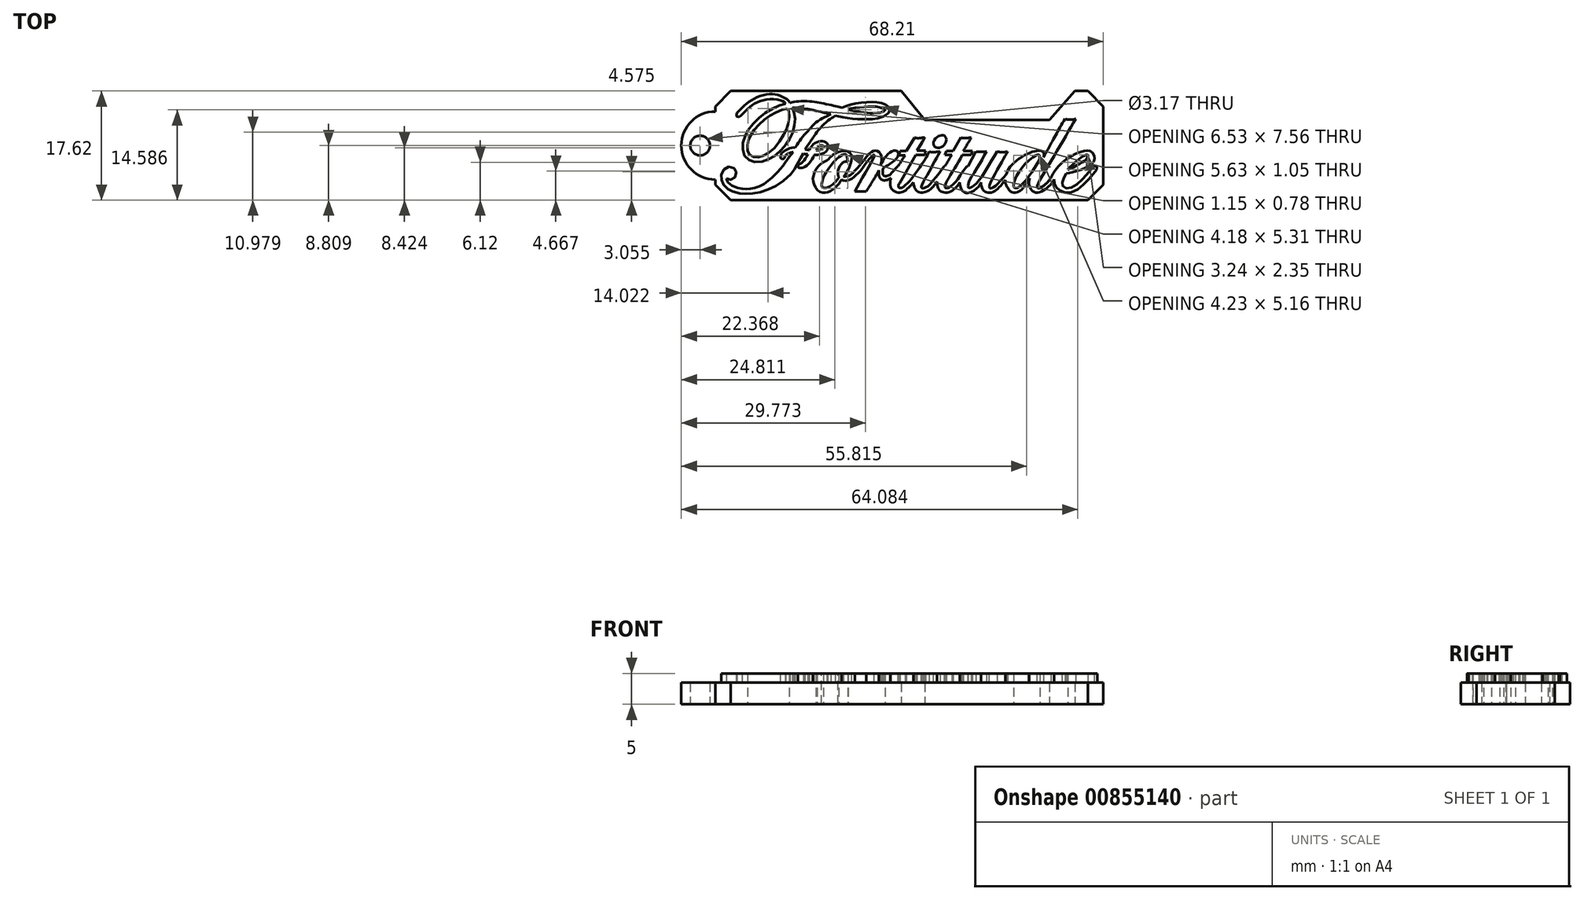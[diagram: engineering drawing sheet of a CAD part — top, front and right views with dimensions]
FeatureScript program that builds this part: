
annotation { "Feature Type Name" : "Feature", "Feature Type Description" : "" }
export const myFeature = defineFeature(function(context is Context, id is Id, definition is map)
    precondition{}
    {
        {
            var Q0;
            Q0=qCreatedBy(makeId("Top.planeOp"),FACE);
            var sketch = newSketch(context, id + "F0", { "sketchPlane" : qUnion([Q0])});
            skFitSpline(sketch, "E0", {"points": [v(-25.9, 14.46) * mm, v(-24.9, 15.47) * mm, v(-23.52, 16.57) * mm, v(-21.48, 17.37) * mm, v(-19.76, 17.48) * mm, v(-18.46, 17.05) * mm, v(-17.47, 16.4) * mm, v(-17.3, 16.1) * mm], "startDerivative": vector(6.68, 6.85) * mm, "endDerivative": vector(1.52, -4.02) * mm});
            skFitSpline(sketch, "E1", {"points": [v(-17.3, 16.1) * mm, v(-16.07, 16.32) * mm, v(-13.99, 16.32) * mm, v(-12.43, 16.1) * mm, v(-10.7, 15.75) * mm, v(-9.45, 15.46) * mm, v(-8.92, 15.33) * mm], "startDerivative": vector(7, 1.67) * mm, "endDerivative": vector(4.54, -1.1) * mm});
            skFitSpline(sketch, "E2", {"points": [v(-8.92, 15.33) * mm, v(-7.8, 15.72) * mm, v(-6.03, 16.1) * mm, v(-4.22, 16.24) * mm, v(-2.81, 16.1) * mm, v(-1.75, 15.75) * mm, v(-1.22, 15.17) * mm, v(-1.42, 14.43) * mm, v(-3.23, 13.6) * mm, v(-4.75, 13.45) * mm, v(-6.34, 13.45) * mm, v(-7.96, 13.65) * mm, v(-9.16, 13.89) * mm, v(-10, 14.03) * mm], "startDerivative": vector(14.5, 5.42) * mm, "endDerivative": vector(-13.1, 2.1) * mm});
            skFitSpline(sketch, "E3", {"points": [v(-10.72, 14.27) * mm, v(-11.87, 14.53) * mm, v(-14.18, 15.04) * mm, v(-15.29, 15.19) * mm, v(-16.51, 15.3) * mm, v(-16.96, 15.28) * mm], "startDerivative": vector(-5.05, 1.09) * mm, "endDerivative": vector(-3.1, -0.28) * mm});
            skFitSpline(sketch, "E4", {"points": [v(-16.96, 15.28) * mm, v(-16.76, 14.83) * mm, v(-16.53, 13.88) * mm, v(-16.54, 13) * mm, v(-16.75, 11.72) * mm, v(-17.21, 10.57) * mm, v(-17.81, 9.59) * mm, v(-18.53, 8.72) * mm, v(-19.73, 7.57) * mm, v(-21, 6.88) * mm, v(-22.1, 6.59) * mm, v(-23.33, 6.61) * mm, v(-24.04, 6.97) * mm, v(-24.7, 7.63) * mm, v(-24.96, 8.7) * mm, v(-24.88, 9.85) * mm, v(-24.48, 10.92) * mm, v(-23.96, 11.89) * mm, v(-22.83, 13.18) * mm, v(-21.63, 14.24) * mm, v(-20.17, 15.17) * mm, v(-18.93, 15.71) * mm, v(-18.07, 15.96) * mm], "startDerivative": vector(6.49, -13.43) * mm, "endDerivative": vector(20.82, 5.37) * mm});
            skFitSpline(sketch, "E5", {"points": [v(-18, 15.96) * mm, v(-18.48, 16.35) * mm, v(-19.96, 16.71) * mm, v(-21.78, 16.5) * mm, v(-23.11, 15.96) * mm, v(-24.23, 15.07) * mm, v(-24.97, 14.28) * mm, v(-25.45, 13.84) * mm, v(-25.72, 13.82) * mm, v(-25.96, 14) * mm, v(-25.9, 14.46) * mm], "startDerivative": vector(-4.62, 4.86) * mm, "endDerivative": vector(2.06, 7.08) * mm});
            skFitSpline(sketch, "E6", {"points": [v(-17.77, 15.15) * mm, v(-19, 14.84) * mm, v(-20.47, 14.1) * mm, v(-22.02, 12.88) * mm, v(-23.32, 11.43) * mm, v(-23.95, 10.22) * mm, v(-24.16, 9.36) * mm, v(-24.13, 8.22) * mm, v(-23.87, 7.8) * mm, v(-23.12, 7.33) * mm, v(-22.13, 7.4) * mm, v(-20.98, 7.9) * mm, v(-19.38, 9.33) * mm, v(-18.07, 11.42) * mm, v(-17.73, 12.26) * mm, v(-17.44, 14.12) * mm, v(-17.62, 15) * mm, v(-17.77, 15.15) * mm]});
            skFitSpline(sketch, "E7", {"points": [v(-10.72, 14.27) * mm, v(-11.48, 13.89) * mm, v(-13.02, 13) * mm, v(-14.3, 11.72) * mm, v(-15.48, 10.35) * mm, v(-16.31, 9.12) * mm, v(-16.48, 8.84) * mm], "startDerivative": vector(-4.97, -2.53) * mm, "endDerivative": vector(-1.64, -2.65) * mm});
            skFitSpline(sketch, "E8", {"points": [v(-16.48, 8.84) * mm, v(-17.1, 8.84) * mm, v(-18.12, 8.39) * mm, v(-18.69, 7.91) * mm, v(-18.87, 7.44) * mm, v(-18.78, 7.13) * mm, v(-18.55, 7) * mm, v(-18.31, 7.08) * mm, v(-18.18, 7.3) * mm, v(-17.96, 7.6) * mm, v(-17.76, 7.85) * mm, v(-17.42, 8.01) * mm, v(-17.05, 8.1) * mm, v(-16.78, 8.15) * mm], "startDerivative": vector(-6.16, 0.8) * mm, "endDerivative": vector(4.12, 0.95) * mm});
            skFitSpline(sketch, "E9", {"points": [v(-16.78, 8.15) * mm, v(-17.38, 7.46) * mm, v(-17.91, 6.68) * mm, v(-18.76, 5.56) * mm, v(-19.67, 4.55) * mm, v(-21.15, 3.25) * mm, v(-23.15, 2.32) * mm, v(-24.75, 2.2) * mm, v(-26.17, 2.48) * mm, v(-26.82, 2.8) * mm, v(-27.23, 3.16) * mm, v(-27.52, 3.62) * mm, v(-27.58, 3.89) * mm], "startDerivative": vector(-8.16, -8.88) * mm, "endDerivative": vector(-0.98, 5.99) * mm});
            skFitSpline(sketch, "E10", {"points": [v(-27.58, 3.89) * mm, v(-27.34, 3.7) * mm, v(-26.64, 3.73) * mm, v(-26.27, 4.04) * mm, v(-26, 4.66) * mm, v(-26.07, 5.08) * mm, v(-26.26, 5.44) * mm, v(-26.74, 5.72) * mm, v(-27.58, 5.67) * mm, v(-28.09, 5.2) * mm, v(-28.39, 4.53) * mm, v(-28.4, 3.92) * mm, v(-28.28, 3.27) * mm, v(-28.04, 2.84) * mm, v(-27.43, 2.22) * mm, v(-26.89, 1.92) * mm, v(-25.9, 1.55) * mm, v(-24.94, 1.4) * mm, v(-24.1, 1.4) * mm, v(-22.97, 1.48) * mm, v(-21.64, 1.78) * mm, v(-20.07, 2.43) * mm, v(-18.7, 3.25) * mm, v(-17.08, 4.7) * mm, v(-16.67, 5.27) * mm, v(-16.3, 5.9) * mm, v(-15.83, 6.72) * mm, v(-15.26, 7.74) * mm, v(-15.15, 7.91) * mm], "startDerivative": vector(8.41, -9.84) * mm, "endDerivative": vector(5.08, 7.16) * mm});
            skFitSpline(sketch, "E11", {"points": [v(-15.15, 7.91) * mm, v(-14.97, 7.84) * mm, v(-14.74, 7.84) * mm, v(-14.44, 7.81) * mm], "startDerivative": vector(0.56, -0.3) * mm, "endDerivative": vector(0.82, -0.1) * mm});
            skFitSpline(sketch, "E12", {"points": [v(-14.44, 7.81) * mm, v(-14.57, 7.49) * mm, v(-15, 6.82) * mm, v(-15.53, 6.32) * mm, v(-15.83, 6.19) * mm, v(-15.96, 6.08) * mm, v(-16.03, 5.86) * mm, v(-15.9, 5.62) * mm, v(-15.6, 5.56) * mm, v(-15.25, 5.65) * mm, v(-14.75, 5.86) * mm, v(-13.9, 6.76) * mm, v(-13.48, 7.48) * mm, v(-13.43, 7.68) * mm], "startDerivative": vector(-1.5, -4.37) * mm, "endDerivative": vector(0.64, 3.35) * mm});
            skFitSpline(sketch, "E13", {"points": [v(-13.43, 7.68) * mm, v(-12.95, 7.68) * mm, v(-12.29, 7.81) * mm, v(-11.5, 8.24) * mm, v(-11.22, 8.72) * mm, v(-11.2, 9.18) * mm, v(-11.34, 9.56) * mm, v(-11.65, 9.8) * mm, v(-12.12, 9.9) * mm, v(-12.69, 9.86) * mm, v(-13.25, 9.6) * mm, v(-13.7, 9.24) * mm, v(-14, 8.8) * mm, v(-14.18, 8.46) * mm], "startDerivative": vector(6.38, -0.23) * mm, "endDerivative": vector(-2.47, -4.89) * mm});
            skFitSpline(sketch, "E14", {"points": [v(-14.18, 8.46) * mm, v(-14.4, 8.51) * mm, v(-14.9, 8.56) * mm], "startDerivative": vector(-0.5, 0.14) * mm, "endDerivative": vector(-0.9, 0.07) * mm});
            skFitSpline(sketch, "E15", {"points": [v(-14.9, 8.56) * mm, v(-14.6, 9.02) * mm, v(-14.12, 9.74) * mm, v(-13.61, 10.44) * mm, v(-12.97, 11.37) * mm, v(-11.47, 12.96) * mm, v(-10.4, 13.76) * mm, v(-10, 14.03) * mm], "startDerivative": vector(2.69, 4.04) * mm, "endDerivative": vector(3.63, 2.41) * mm});
            skFitSpline(sketch, "E16", {"points": [v(-13.1, 8.44) * mm, v(-12.86, 8.84) * mm, v(-12.6, 9.06) * mm, v(-12.3, 9.2) * mm, v(-12, 9.16) * mm, v(-11.91, 9.03) * mm, v(-12, 8.82) * mm, v(-12.19, 8.63) * mm, v(-12.53, 8.47) * mm, v(-12.96, 8.42) * mm], "startDerivative": vector(1.62, 3.25) * mm, "endDerivative": vector(-3.32, -0.15) * mm});
            skFitSpline(sketch, "E17", {"points": [v(-12.96, 8.42) * mm, v(-13.1, 8.44) * mm], "startDerivative": vector(-0.14, 0.02) * mm, "endDerivative": vector(-0.14, 0.02) * mm});
            skFitSpline(sketch, "E18", {"points": [v(-7.93, 15.04) * mm, v(-7.1, 15.24) * mm, v(-5.76, 15.43) * mm, v(-4.6, 15.5) * mm, v(-3.4, 15.47) * mm, v(-2.45, 15.24) * mm, v(-1.95, 14.98) * mm, v(-2.02, 14.85) * mm, v(-2.26, 14.72) * mm, v(-2.6, 14.56) * mm, v(-2.88, 14.49) * mm, v(-3.54, 14.45) * mm, v(-4.4, 14.44) * mm, v(-5.03, 14.5) * mm, v(-5.97, 14.63) * mm, v(-6.66, 14.75) * mm, v(-7.62, 14.91) * mm, v(-7.93, 15.04) * mm]});
            skFitSpline(sketch, "E19", {"points": [v(-11.34, 6.78) * mm, v(-12.14, 6.36) * mm, v(-13, 5.56) * mm, v(-13.56, 4.23) * mm, v(-13.5, 3.23) * mm, v(-12.79, 1.93) * mm, v(-11.89, 1.6) * mm, v(-10.96, 1.76) * mm, v(-10.06, 2.33) * mm, v(-9.37, 3.13) * mm, v(-9, 3.71) * mm], "startDerivative": vector(-8.7, -4) * mm, "endDerivative": vector(4.14, 6.88) * mm});
            skFitSpline(sketch, "E20", {"points": [v(-11.34, 6.78) * mm, v(-10.7, 7.4) * mm, v(-9.66, 8.1) * mm, v(-8.28, 8.35) * mm, v(-7.53, 7.93) * mm, v(-7.35, 7.05) * mm, v(-7.6, 6) * mm, v(-8.22, 4.77) * mm, v(-8.7, 4.13) * mm], "startDerivative": vector(5.23, 5.36) * mm, "endDerivative": vector(-4.35, -5.22) * mm});
            skFitSpline(sketch, "E21", {"points": [v(-8, 6.63) * mm, v(-8.07, 7.24) * mm, v(-8.17, 7.6) * mm, v(-8.54, 7.79) * mm, v(-9.4, 7.35) * mm, v(-10.6, 6.12) * mm, v(-11.63, 4.61) * mm, v(-12.08, 3.55) * mm, v(-12.18, 2.56) * mm, v(-11.9, 2.33) * mm, v(-11.04, 2.46) * mm, v(-9.8, 3.5) * mm, v(-9.43, 4.03) * mm], "startDerivative": vector(-1.3, 9.27) * mm, "endDerivative": vector(4.03, 6.68) * mm});
            skFitSpline(sketch, "E22", {"points": [v(-9.43, 4.03) * mm, v(-9.53, 4.39) * mm, v(-9.53, 5.3) * mm, v(-9.11, 6.12) * mm, v(-8.66, 6.53) * mm, v(-8, 6.63) * mm], "startDerivative": vector(-0.69, 2.08) * mm, "endDerivative": vector(3.63, 0.09) * mm});
            skFitSpline(sketch, "E23", {"points": [v(-8.7, 4.13) * mm, v(-7.75, 4.34) * mm, v(-6.64, 5.33) * mm, v(-5.55, 6.63) * mm, v(-4.65, 7.73) * mm, v(-3.8, 8.36) * mm, v(-3.13, 8.27) * mm, v(-2.66, 7.84) * mm, v(-2.5, 7) * mm, v(-2.72, 5.96) * mm], "startDerivative": vector(9.04, 0.75) * mm, "endDerivative": vector(-2.78, -9.43) * mm});
            skFitSpline(sketch, "E24", {"points": [v(-2.72, 5.96) * mm, v(-2.3, 6.78) * mm, v(-1.3, 7.98) * mm, v(-0.43, 8.38) * mm, v(0.06, 8.2) * mm, v(0.18, 7.68) * mm, v(-0.35, 6.88) * mm, v(-1.62, 5.96) * mm, v(-2.2, 5.62) * mm], "startDerivative": vector(2.82, 6.13) * mm, "endDerivative": vector(-4.83, -2.64) * mm});
            skFitSpline(sketch, "E25", {"points": [v(-2.2, 5.62) * mm, v(-2.32, 5.27) * mm, v(-2.33, 4.67) * mm, v(-2.08, 4.3) * mm, v(-1.49, 4.32) * mm, v(-0.98, 4.68) * mm, v(-0.34, 5.4) * mm, v(0.03, 5.78) * mm, v(0.16, 5.86) * mm], "startDerivative": vector(-1.27, -3) * mm, "endDerivative": vector(1.86, 0.75) * mm});
            skFitSpline(sketch, "E26", {"points": [v(0.16, 5.86) * mm, v(0.73, 6.78) * mm, v(1.3, 7.65) * mm], "startDerivative": vector(1.1, 1.84) * mm, "endDerivative": vector(1.16, 1.75) * mm});
            skLineSegment(sketch, "E27", {"start": v(1.3, 7.65) * mm, "end": v(0.26, 7.65) * mm});
            skLineSegment(sketch, "E28", {"start": v(0.26, 7.65) * mm, "end": v(0.5, 8.35) * mm});
            skLineSegment(sketch, "E29", {"start": v(0.5, 8.35) * mm, "end": v(1.5, 8.35) * mm});
            skLineSegment(sketch, "E30", {"start": v(1.5, 8.35) * mm, "end": v(2.81, 10.5) * mm});
            skFitSpline(sketch, "E31", {"points": [v(2.81, 10.5) * mm, v(3.28, 10.39) * mm, v(4.23, 10.5) * mm], "startDerivative": vector(1.03, -0.37) * mm, "endDerivative": vector(1.76, 0.33) * mm});
            skLineSegment(sketch, "E32", {"start": v(4.23, 10.5) * mm, "end": v(4.49, 10.56) * mm});
            skLineSegment(sketch, "E33", {"start": v(4.49, 10.56) * mm, "end": v(4, 9.71) * mm});
            skLineSegment(sketch, "E34", {"start": v(4, 9.71) * mm, "end": v(3.23, 8.38) * mm});
            skLineSegment(sketch, "E35", {"start": v(3.23, 8.38) * mm, "end": v(4.62, 8.38) * mm});
            skLineSegment(sketch, "E36", {"start": v(4.62, 8.38) * mm, "end": v(4.46, 7.72) * mm});
            skLineSegment(sketch, "E37", {"start": v(4.46, 7.72) * mm, "end": v(3.01, 7.72) * mm});
            skLineSegment(sketch, "E38", {"start": v(3.01, 7.72) * mm, "end": v(0.37, 3.14) * mm});
            skFitSpline(sketch, "E39", {"points": [v(0.37, 3.14) * mm, v(0.23, 2.83) * mm, v(0.24, 2.46) * mm, v(0.6, 2.35) * mm, v(1.33, 2.78) * mm, v(2.9, 4.63) * mm, v(4.62, 7.19) * mm, v(5.16, 8.24) * mm], "startDerivative": vector(-1.96, -3.45) * mm, "endDerivative": vector(2.89, 6.1) * mm});
            skFitSpline(sketch, "E40", {"points": [v(5.16, 8.24) * mm, v(5.41, 8.15) * mm, v(6.1, 8.15) * mm, v(6.94, 8.24) * mm], "startDerivative": vector(0.95, -0.43) * mm, "endDerivative": vector(2.04, 0.26) * mm});
            skFitSpline(sketch, "E41", {"points": [v(7.2, 10.84) * mm, v(6.54, 10.65) * mm, v(5.92, 9.9) * mm, v(5.93, 9.21) * mm, v(6.4, 8.84) * mm, v(7.19, 8.98) * mm, v(7.81, 9.6) * mm, v(7.92, 10.32) * mm, v(7.67, 10.76) * mm, v(7.2, 10.84) * mm]});
            skFitSpline(sketch, "E42", {"points": [v(6.94, 8.24) * mm, v(5.89, 6.32) * mm, v(4.68, 4.14) * mm, v(3.94, 2.7) * mm, v(3.98, 2.37) * mm, v(4.2, 2.29) * mm, v(4.62, 2.42) * mm, v(5.27, 2.93) * mm, v(7.32, 5.45) * mm, v(7.57, 5.85) * mm], "startDerivative": vector(-6.56, -11.95) * mm, "endDerivative": vector(2.07, 3.87) * mm});
            skFitSpline(sketch, "E43", {"points": [v(7.57, 5.85) * mm, v(7.73, 5.87) * mm], "startDerivative": vector(0.16, 0.03) * mm, "endDerivative": vector(0.16, 0.03) * mm});
            skFitSpline(sketch, "E44", {"points": [v(7.73, 5.87) * mm, v(8.4, 7) * mm, v(8.83, 7.68) * mm], "startDerivative": vector(1.24, 2.13) * mm, "endDerivative": vector(0.94, 1.47) * mm});
            skFitSpline(sketch, "E45", {"points": [v(8.83, 7.68) * mm, v(7.73, 7.68) * mm], "startDerivative": vector(-1.1, 0) * mm, "endDerivative": vector(-1.1, 0) * mm});
            skFitSpline(sketch, "E46", {"points": [v(7.73, 7.68) * mm, v(7.96, 8.35) * mm], "startDerivative": vector(0.23, 0.66) * mm, "endDerivative": vector(0.23, 0.66) * mm});
            skFitSpline(sketch, "E47", {"points": [v(7.96, 8.35) * mm, v(9.02, 8.35) * mm], "startDerivative": vector(1.06, 0) * mm, "endDerivative": vector(1.06, 0) * mm});
            skFitSpline(sketch, "E48", {"points": [v(9.02, 8.35) * mm, v(10.34, 10.54) * mm], "startDerivative": vector(1.32, 2.19) * mm, "endDerivative": vector(1.32, 2.19) * mm});
            skFitSpline(sketch, "E49", {"points": [v(10.34, 10.54) * mm, v(10.48, 10.44) * mm, v(11.31, 10.43) * mm, v(11.98, 10.47) * mm], "startDerivative": vector(0.5, -0.58) * mm, "endDerivative": vector(1.58, 0.1) * mm});
            skFitSpline(sketch, "E50", {"points": [v(11.98, 10.47) * mm, v(11.42, 9.56) * mm, v(10.72, 8.35) * mm], "startDerivative": vector(-1.18, -1.88) * mm, "endDerivative": vector(-1.34, -2.36) * mm});
            skFitSpline(sketch, "E51", {"points": [v(10.72, 8.35) * mm, v(12.17, 8.35) * mm], "startDerivative": vector(1.45, 0) * mm, "endDerivative": vector(1.45, 0) * mm});
            skFitSpline(sketch, "E52", {"points": [v(12.17, 8.35) * mm, v(11.98, 7.68) * mm], "startDerivative": vector(-0.2, -0.66) * mm, "endDerivative": vector(-0.2, -0.66) * mm});
            skFitSpline(sketch, "E53", {"points": [v(11.98, 7.68) * mm, v(10.53, 7.68) * mm], "startDerivative": vector(-1.45, 0) * mm, "endDerivative": vector(-1.45, 0) * mm});
            skFitSpline(sketch, "E54", {"points": [v(10.53, 7.68) * mm, v(9.36, 5.67) * mm, v(8.24, 3.83) * mm, v(7.8, 2.88) * mm, v(7.73, 2.4) * mm, v(8.1, 2.3) * mm, v(8.75, 2.67) * mm, v(9.88, 3.91) * mm, v(11.27, 5.85) * mm, v(11.43, 5.85) * mm], "startDerivative": vector(-7.03, -12.37) * mm, "endDerivative": vector(3.22, -1.43) * mm});
            skFitSpline(sketch, "E55", {"points": [v(11.43, 5.85) * mm, v(12.73, 8.24) * mm], "startDerivative": vector(1.3, 2.39) * mm, "endDerivative": vector(1.3, 2.39) * mm});
            skFitSpline(sketch, "E56", {"points": [v(12.73, 8.24) * mm, v(13.08, 8.18) * mm, v(13.83, 8.18) * mm, v(14.44, 8.24) * mm], "startDerivative": vector(1.17, -0.27) * mm, "endDerivative": vector(1.64, 0.18) * mm});
            skFitSpline(sketch, "E57", {"points": [v(14.44, 8.24) * mm, v(13.06, 5.81) * mm, v(11.68, 3.53) * mm, v(11.52, 3.05) * mm, v(11.49, 2.57) * mm, v(11.6, 2.33) * mm, v(12.05, 2.47) * mm, v(13.1, 3.42) * mm, v(14.44, 5.38) * mm, v(16.12, 8.24) * mm], "startDerivative": vector(-7.94, -14.59) * mm, "endDerivative": vector(9.89, 17.01) * mm});
            skFitSpline(sketch, "E58", {"points": [v(16.12, 8.24) * mm, v(16.53, 8.16) * mm, v(17.4, 8.16) * mm, v(17.86, 8.24) * mm], "startDerivative": vector(1.24, -0.31) * mm, "endDerivative": vector(1.33, 0.3) * mm});
            skFitSpline(sketch, "E59", {"points": [v(17.86, 8.24) * mm, v(17.05, 6.8) * mm, v(15.38, 3.82) * mm, v(14.92, 2.76) * mm, v(14.94, 2.33) * mm, v(15.25, 2.3) * mm, v(16, 2.78) * mm, v(17.26, 4.12) * mm, v(17.63, 4.54) * mm], "startDerivative": vector(-4.51, -8.17) * mm, "endDerivative": vector(3.5, 3.82) * mm});
            skFitSpline(sketch, "E60", {"points": [v(17.63, 4.54) * mm, v(18.1, 5.58) * mm, v(19.63, 7.02) * mm, v(21.68, 8.12) * mm, v(22.88, 8.37) * mm, v(23.49, 8.24) * mm, v(23.73, 7.7) * mm, v(23.66, 7.32) * mm], "startDerivative": vector(2.37, 7.02) * mm, "endDerivative": vector(-0.17, -4.12) * mm});
            skFitSpline(sketch, "E61", {"points": [v(23.66, 7.32) * mm, v(24.63, 9.1) * mm, v(27.11, 13.55) * mm], "startDerivative": vector(1.98, 4.13) * mm, "endDerivative": vector(4.56, 8.03) * mm});
            skFitSpline(sketch, "E62", {"points": [v(27.11, 13.55) * mm, v(27.61, 13.4) * mm, v(28.58, 13.44) * mm, v(28.87, 13.55) * mm], "startDerivative": vector(1.33, -0.57) * mm, "endDerivative": vector(0.91, 0.48) * mm});
            skFitSpline(sketch, "E63", {"points": [v(28.87, 13.55) * mm, v(26.97, 10.27) * mm, v(24.32, 5.8) * mm, v(22.73, 2.97) * mm, v(22.65, 2.42) * mm, v(22.85, 2.27) * mm, v(22.87, 2.27) * mm, v(23.66, 2.7) * mm, v(24.86, 4.01) * mm], "startDerivative": vector(-8.97, -15.56) * mm, "endDerivative": vector(7.05, 10.8) * mm});
            skFitSpline(sketch, "E64", {"points": [v(24.86, 4.01) * mm, v(25.87, 5.63) * mm, v(27.9, 7.37) * mm, v(30.07, 8.31) * mm, v(31.07, 8.35) * mm, v(31.75, 7.8) * mm, v(31.92, 7) * mm, v(31.44, 6.2) * mm, v(30.08, 5.44) * mm, v(28.23, 4.87) * mm, v(27.32, 4.67) * mm], "startDerivative": vector(7.5, 14.08) * mm, "endDerivative": vector(-10.22, -2.07) * mm});
            skFitSpline(sketch, "E65", {"points": [v(27.57, 5.33) * mm, v(28.8, 6.55) * mm, v(30.14, 7.53) * mm, v(30.81, 7.7) * mm, v(30.6, 7.03) * mm, v(29.37, 6.18) * mm, v(27.57, 5.33) * mm]});
            skFitSpline(sketch, "E66", {"points": [v(27.32, 4.67) * mm, v(26.83, 3.71) * mm, v(26.68, 2.85) * mm, v(27.1, 2.38) * mm, v(28.36, 2.46) * mm, v(30.01, 3.84) * mm, v(31.15, 5.17) * mm, v(31.58, 5.71) * mm, v(31.9, 5.9) * mm, v(32.21, 5.8) * mm, v(32.32, 5.52) * mm, v(32.1, 5.13) * mm, v(30.9, 3.71) * mm, v(28.92, 1.96) * mm, v(27.09, 1.58) * mm, v(25.83, 2.3) * mm, v(25.48, 2.96) * mm, v(25.35, 3.74) * mm], "startDerivative": vector(-8.8, -15.61) * mm, "endDerivative": vector(-2.02, 15.64) * mm});
            skFitSpline(sketch, "E67", {"points": [v(25.35, 3.74) * mm, v(24.85, 2.97) * mm, v(23.93, 2.16) * mm, v(22.7, 1.6) * mm, v(21.8, 1.95) * mm, v(21.45, 2.54) * mm, v(21.29, 3.15) * mm, v(21.45, 3.92) * mm], "startDerivative": vector(-3.09, -5.5) * mm, "endDerivative": vector(1.9, 6.01) * mm});
            skFitSpline(sketch, "E68", {"points": [v(22.45, 7.64) * mm, v(20.76, 6.28) * mm, v(19.32, 4.32) * mm, v(18.8, 2.82) * mm, v(18.97, 2.35) * mm, v(19.45, 2.4) * mm, v(20.45, 3.2) * mm, v(22, 5.3) * mm, v(22.95, 6.88) * mm, v(23.04, 7.45) * mm, v(22.95, 7.7) * mm, v(22.45, 7.64) * mm]});
            skFitSpline(sketch, "E69", {"points": [v(21.45, 3.92) * mm, v(20.61, 2.65) * mm, v(19.6, 1.73) * mm, v(18.51, 1.68) * mm, v(17.86, 2.34) * mm, v(17.49, 3.26) * mm, v(17.49, 3.65) * mm], "startDerivative": vector(-3.9, -6.35) * mm, "endDerivative": vector(0.42, 3.4) * mm});
            skFitSpline(sketch, "E70", {"points": [v(17.49, 3.65) * mm, v(16.8, 2.78) * mm, v(15.4, 1.68) * mm, v(14.2, 1.73) * mm, v(13.64, 2.55) * mm, v(13.55, 3.26) * mm], "startDerivative": vector(-3.04, -4.14) * mm, "endDerivative": vector(-0.17, 4.26) * mm});
            skFitSpline(sketch, "E71", {"points": [v(13.55, 3.26) * mm, v(13, 2.42) * mm, v(12, 1.7) * mm, v(10.86, 1.61) * mm, v(10.23, 2.53) * mm, v(10.1, 3.26) * mm], "startDerivative": vector(-2.37, -4.4) * mm, "endDerivative": vector(-0.31, 4.03) * mm});
            skFitSpline(sketch, "E72", {"points": [v(10.1, 3.26) * mm, v(9.53, 2.43) * mm, v(8.4, 1.7) * mm, v(7.2, 1.72) * mm, v(6.66, 2.26) * mm, v(6.48, 3.03) * mm, v(6.43, 3.4) * mm], "startDerivative": vector(-2.79, -4.67) * mm, "endDerivative": vector(-0.47, 2.97) * mm});
            skFitSpline(sketch, "E73", {"points": [v(6.43, 3.4) * mm, v(5.8, 2.54) * mm, v(4.57, 1.7) * mm, v(3.53, 1.68) * mm, v(2.93, 2.14) * mm, v(2.65, 2.88) * mm, v(2.64, 3.26) * mm], "startDerivative": vector(-2.87, -4.66) * mm, "endDerivative": vector(0.15, 3.12) * mm});
            skFitSpline(sketch, "E74", {"points": [v(2.64, 3.26) * mm, v(2.1, 2.66) * mm, v(1.28, 1.91) * mm, v(0.58, 1.63) * mm, v(-0.2, 1.68) * mm, v(-0.86, 2.13) * mm, v(-1.11, 2.88) * mm, v(-1.12, 3.53) * mm, v(-0.97, 3.92) * mm], "startDerivative": vector(-3.93, -4.32) * mm, "endDerivative": vector(1.98, 3.82) * mm});
            skFitSpline(sketch, "E75", {"points": [v(-0.97, 3.92) * mm, v(-1.63, 3.65) * mm, v(-2.45, 3.65) * mm, v(-2.91, 4.22) * mm, v(-2.98, 4.92) * mm, v(-2.93, 5.23) * mm], "startDerivative": vector(-2.92, -1.41) * mm, "endDerivative": vector(0.41, 1.98) * mm});
            skFitSpline(sketch, "E76", {"points": [v(-2.93, 5.23) * mm, v(-3.74, 3.8) * mm, v(-5.01, 1.76) * mm], "startDerivative": vector(-1.67, -3.03) * mm, "endDerivative": vector(-2.46, -3.88) * mm});
            skFitSpline(sketch, "E77", {"points": [v(-5.01, 1.76) * mm, v(-6.86, 1.76) * mm], "startDerivative": vector(-1.85, 0) * mm, "endDerivative": vector(-1.85, 0) * mm});
            skFitSpline(sketch, "E78", {"points": [v(-6.86, 1.76) * mm, v(-5.73, 3.8) * mm, v(-4.27, 6.35) * mm, v(-3.77, 7.36) * mm, v(-3.73, 7.7) * mm, v(-3.97, 7.56) * mm, v(-4.67, 6.84) * mm, v(-5.48, 5.72) * mm, v(-6.25, 4.78) * mm, v(-6.67, 4.37) * mm, v(-7.22, 3.92) * mm, v(-8.07, 3.53) * mm, v(-8.7, 3.53) * mm, v(-9, 3.71) * mm], "startDerivative": vector(8.67, 15.91) * mm, "endDerivative": vector(-5.7, 4.44) * mm});
            skLineSegment(sketch, "E79.bottom", {"start": v(-29.4, 18.01) * mm, "end": v(0.67, 18.01) * mm});
            skLineSegment(sketch, "E79.top", {"start": v(-29.4, 0.39) * mm, "end": v(33.32, 0.39) * mm});
            skLineSegment(sketch, "E79.left", {"start": v(-29.4, 18.01) * mm, "end": v(-29.4, 14.7) * mm});
            skLineSegment(sketch, "E79.right", {"start": v(33.32, 18.01) * mm, "end": v(33.32, 0.39) * mm});
            skLineSegment(sketch, "E80", {"start": v(-18.07, 15.96) * mm, "end": v(-18, 15.96) * mm});
            skPoint(sketch, "E81.center.orphan", {"position": v(-29.4, 9.2) * mm});
            skArc(sketch, "E82.trimOffspring", {"start": v(-29.4, 14.7) * mm, "mid": v(-34.9, 9.2) * mm, "end": v(-29.4, 3.7) * mm});
            skCircle(sketch, "E83", {"center": v(-31.83, 9.2) * mm, "radius": 1.59 * mm});
            skLineSegment(sketch, "E84.trimOffspring", {"start": v(-29.4, 3.7) * mm, "end": v(-29.4, 0.39) * mm});
            skLineSegment(sketch, "E85", {"start": v(0.67, 18.01) * mm, "end": v(4.45, 13.36) * mm});
            skLineSegment(sketch, "E86", {"start": v(4.45, 13.36) * mm, "end": v(24.62, 13.36) * mm});
            skLineSegment(sketch, "E87", {"start": v(24.62, 13.36) * mm, "end": v(28.7, 18.01) * mm});
            skLineSegment(sketch, "E88.trimOffspring", {"start": v(28.7, 18.01) * mm, "end": v(33.32, 18.01) * mm});
            skSolve(sketch);
        }
        {
            var Q0;
            Q0=makeQuery(id+"F0.imprint","IMPRINT",FACE,{"disambiguationData":[TD([[makeQuery(id+"F0.imprint","IMPRINT",EDGE,{"derivedFrom":sQuery(id+"F0.wireOp",EDGE,"E0")}),-1.0]])]});
            var Q1;
            Q1=makeQuery(id+"F0.imprint","IMPRINT",FACE,{"disambiguationData":[TD([[makeQuery(id+"F0.imprint","IMPRINT",EDGE,{"derivedFrom":sQuery(id+"F0.wireOp",EDGE,"E19")}),1.0]])]});
            var Q2;
            Q2=makeQuery(id+"F0.imprint","IMPRINT",FACE,{"disambiguationData":[TD([[makeQuery(id+"F0.imprint","IMPRINT",EDGE,{"derivedFrom":sQuery(id+"F0.wireOp",EDGE,"E41")}),1.0]])]});
            extrude(context, id + "F1", {"entities" : qUnion([Q0, Q1, Q2]), "depth" : 5 * mm, "offsetDistance" : 25 * mm});
        }
        {
            var Q0;
            Q0=makeQuery(id+"F0.imprint","IMPRINT",FACE,{"disambiguationData":[TD([[makeQuery(id+"F0.imprint","IMPRINT",EDGE,{"derivedFrom":sQuery(id+"F0.wireOp",EDGE,"E0")}),1.0]])]});
            extrude(context, id + "F2", {"entities" : qUnion([Q0]), "operationType" : NewBodyOperationType.ADD, "depth" : 3.5 * mm, "offsetDistance" : 25 * mm});
        }
        {
            var Q0;
            Q0=makeQuery(id+"F2.opExtrude","SWEPT_EDGE",EDGE,{"disambiguationData":[OSD([sQuery(id+"F0.wireOp",EDGE,"E79.bottom"),sQuery(id+"F0.wireOp",EDGE,"E79.left")])]});
            var Q1;
            Q1=makeQuery(id+"F2.opExtrude","SWEPT_EDGE",EDGE,{"disambiguationData":[OSD([sQuery(id+"F0.wireOp",EDGE,"E79.top"),sQuery(id+"F0.wireOp",EDGE,"E79.right")])]});
            var Q2;
            Q2=makeQuery(id+"F2.opExtrude","SWEPT_EDGE",EDGE,{"disambiguationData":[OSD([sQuery(id+"F0.wireOp",EDGE,"E79.right"),sQuery(id+"F0.wireOp",EDGE,"E88.trimOffspring")])]});
            var Q3;
            Q3=makeQuery(id+"F2.opExtrude","SWEPT_EDGE",EDGE,{"disambiguationData":[OSD([sQuery(id+"F0.wireOp",EDGE,"E79.top"),sQuery(id+"F0.wireOp",EDGE,"E84.trimOffspring")])]});
            chamfer(context, id + "F3", {"entities" : qUnion([Q0, Q1, Q2, Q3]), "width" : 2.5 * mm, "tangentPropagation" : true});
        }
    });
